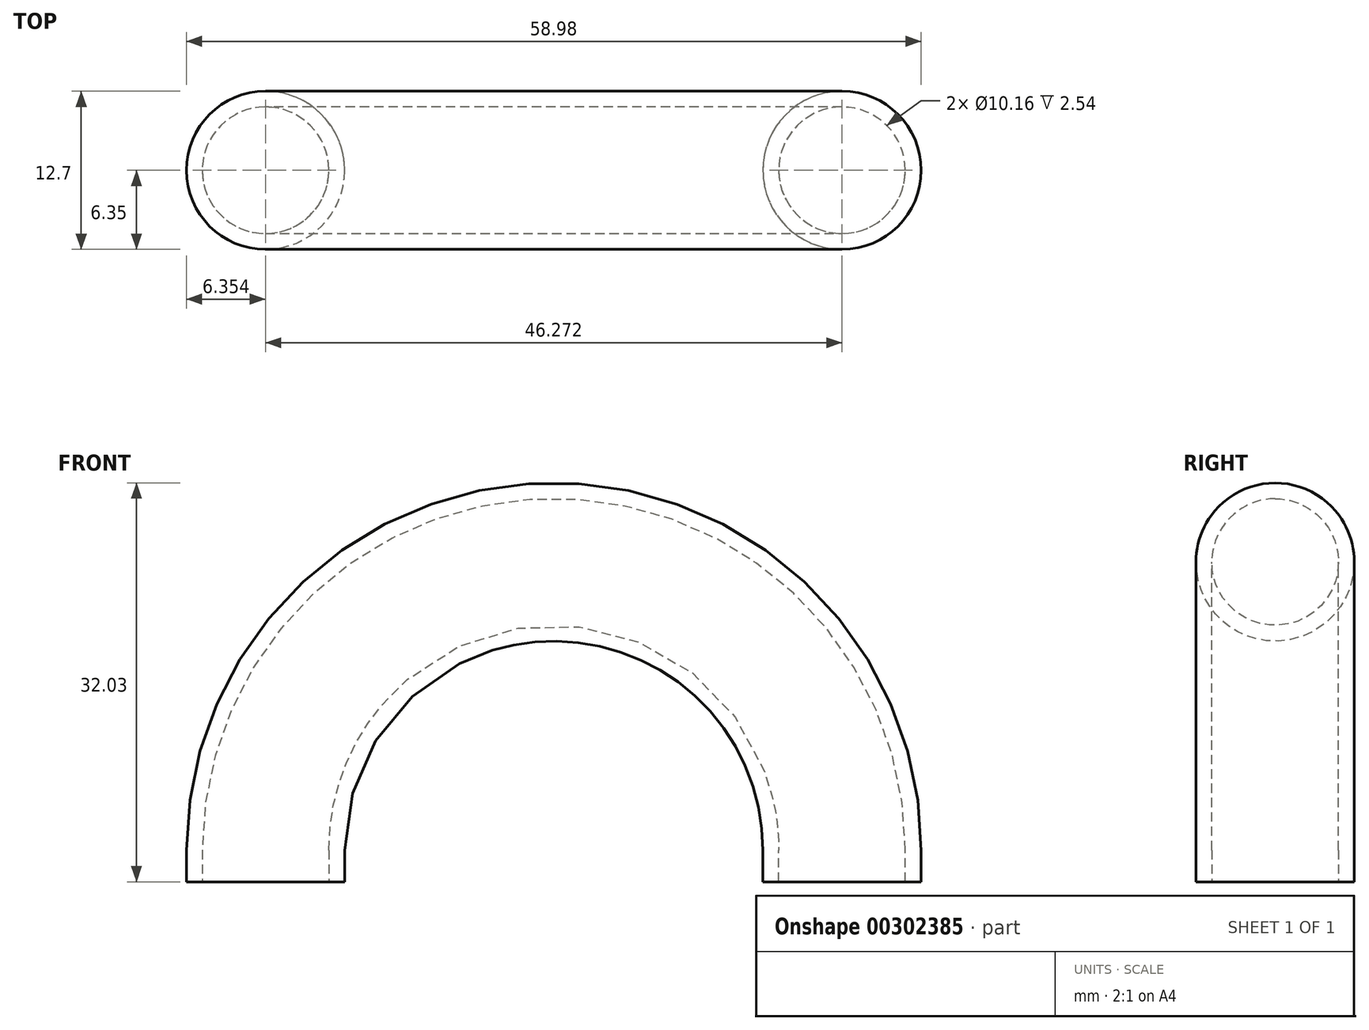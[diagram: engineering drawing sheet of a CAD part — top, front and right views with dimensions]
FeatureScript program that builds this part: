
annotation { "Feature Type Name" : "Feature", "Feature Type Description" : "" }
export const myFeature = defineFeature(function(context is Context, id is Id, definition is map)
    precondition{}
    {
        {
            var Q0;
            Q0=qCreatedBy(makeId("Front.planeOp"),FACE);
            var sketch = newSketch(context, id + "F0", { "sketchPlane" : qUnion([Q0])});
            skLineSegment(sketch, "E0.0", {"start": v(-23.14, 0) * mm, "end": v(-23.14, 2.54) * mm});
            skLineSegment(sketch, "E1.0", {"start": v(23.14, 0) * mm, "end": v(23.14, 2.54) * mm});
            skArc(sketch, "E2", {"start": v(-23.14, 2.54) * mm, "mid": v(0, 25.68) * mm, "end": v(23.14, 2.54) * mm});
            skSolve(sketch);
        }
        {
            var Q0;
            Q0=qCreatedBy(makeId("Top.planeOp"),FACE);
            var sketch = newSketch(context, id + "F1", { "sketchPlane" : qUnion([Q0])});
            skCircle(sketch, "E3", {"center": v(23.14, 0) * mm, "radius": 6.35 * mm});
            skSolve(sketch);
        }
        {
            var Q0;
            Q0 = qSketchRegion(id + "F1", true);
            var Q1;
            Q1 = qConstructionFilter(qBodyType(qCreatedBy(id + "F0" ,EDGE), BodyType.WIRE), ConstructionObject.NO);
            sweep(context, id + "F2", {"profiles" : qUnion([Q0]), "path" : qUnion([Q1])});
        }
        {
            var Q0;
            Q0=makeQuery(id+"F2.opSweep","CAP_FACE",FACE,{"disambiguationData":[OSD([sQuery(id+"F0.wireOp",VERTEX,"E0.0.start"),sQuery(id+"F1.wireOp",EDGE,"E3")])],"isStart":false});
            var Q1;
            Q1=makeQuery(id+"F2.opSweep","CAP_FACE",FACE,{"disambiguationData":[OSD([sQuery(id+"F0.wireOp",VERTEX,"E1.0.start"),sQuery(id+"F1.wireOp",EDGE,"E3")])],"isStart":true});
            shell(context, id + "F3", {"entities" : qUnion([Q0, Q1]), "thickness" : 1.27 * mm});
        }
    });
